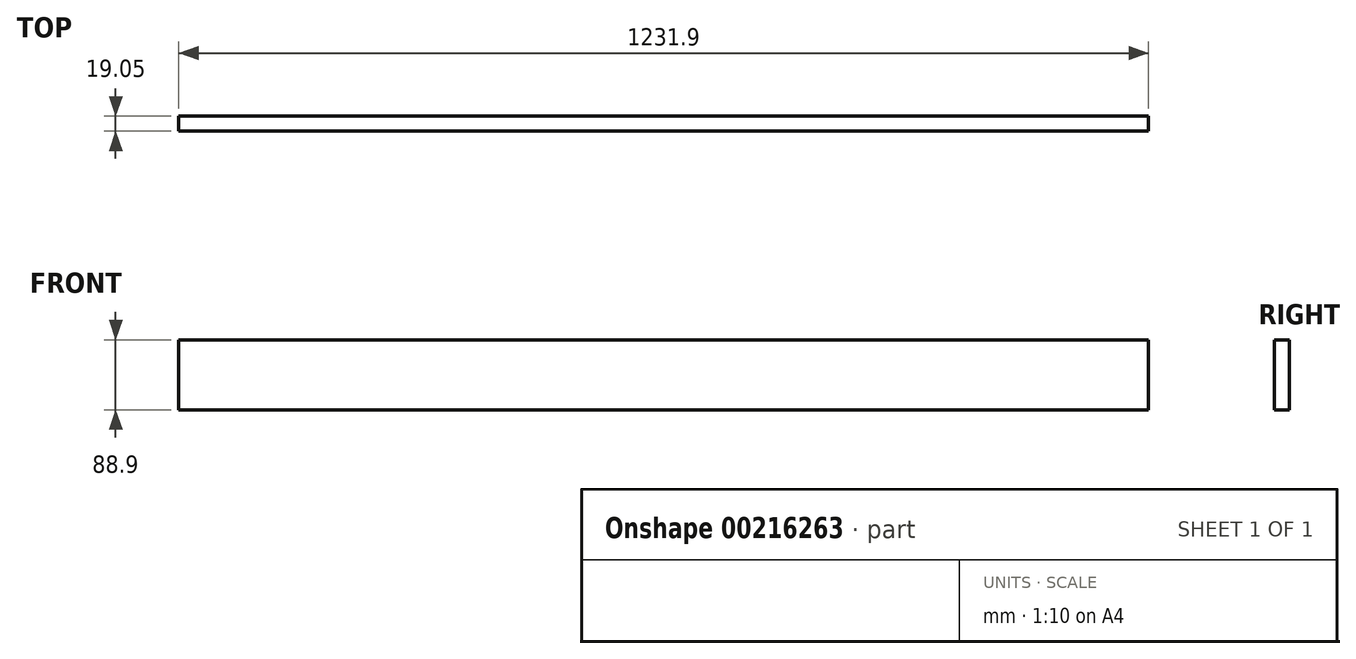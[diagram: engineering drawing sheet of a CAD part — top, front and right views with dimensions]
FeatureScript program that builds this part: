
annotation { "Feature Type Name" : "Feature", "Feature Type Description" : "" }
export const myFeature = defineFeature(function(context is Context, id is Id, definition is map)
    precondition{}
    {
        {
            var Q0;
            Q0=qCreatedBy(makeId("Front.planeOp"),FACE);
            var sketch = newSketch(context, id + "F0", { "sketchPlane" : qUnion([Q0])});
            skLineSegment(sketch, "E0", {"start": v(-4643.85, -526.66) * mm, "end": v(-3411.95, -526.66) * mm});
            skLineSegment(sketch, "E1", {"start": v(-3411.95, -526.66) * mm, "end": v(-3411.95, -615.56) * mm});
            skLineSegment(sketch, "E2", {"start": v(-3411.95, -615.56) * mm, "end": v(-4643.85, -615.56) * mm});
            skLineSegment(sketch, "E3", {"start": v(-4643.85, -615.56) * mm, "end": v(-4643.85, -526.66) * mm});
            skSolve(sketch);
        }
        {
            var Q0;
            Q0=makeQuery(id+"F0.imprint","IMPRINT",FACE,{"disambiguationData":[TD([[makeQuery(id+"F0.imprint","IMPRINT",EDGE,{"derivedFrom":sQuery(id+"F0.wireOp",EDGE,"E0")}),-1.0]])]});
            extrude(context, id + "F1", {"entities" : qUnion([Q0]), "depth" : 19.05 * mm});
        }
    });
